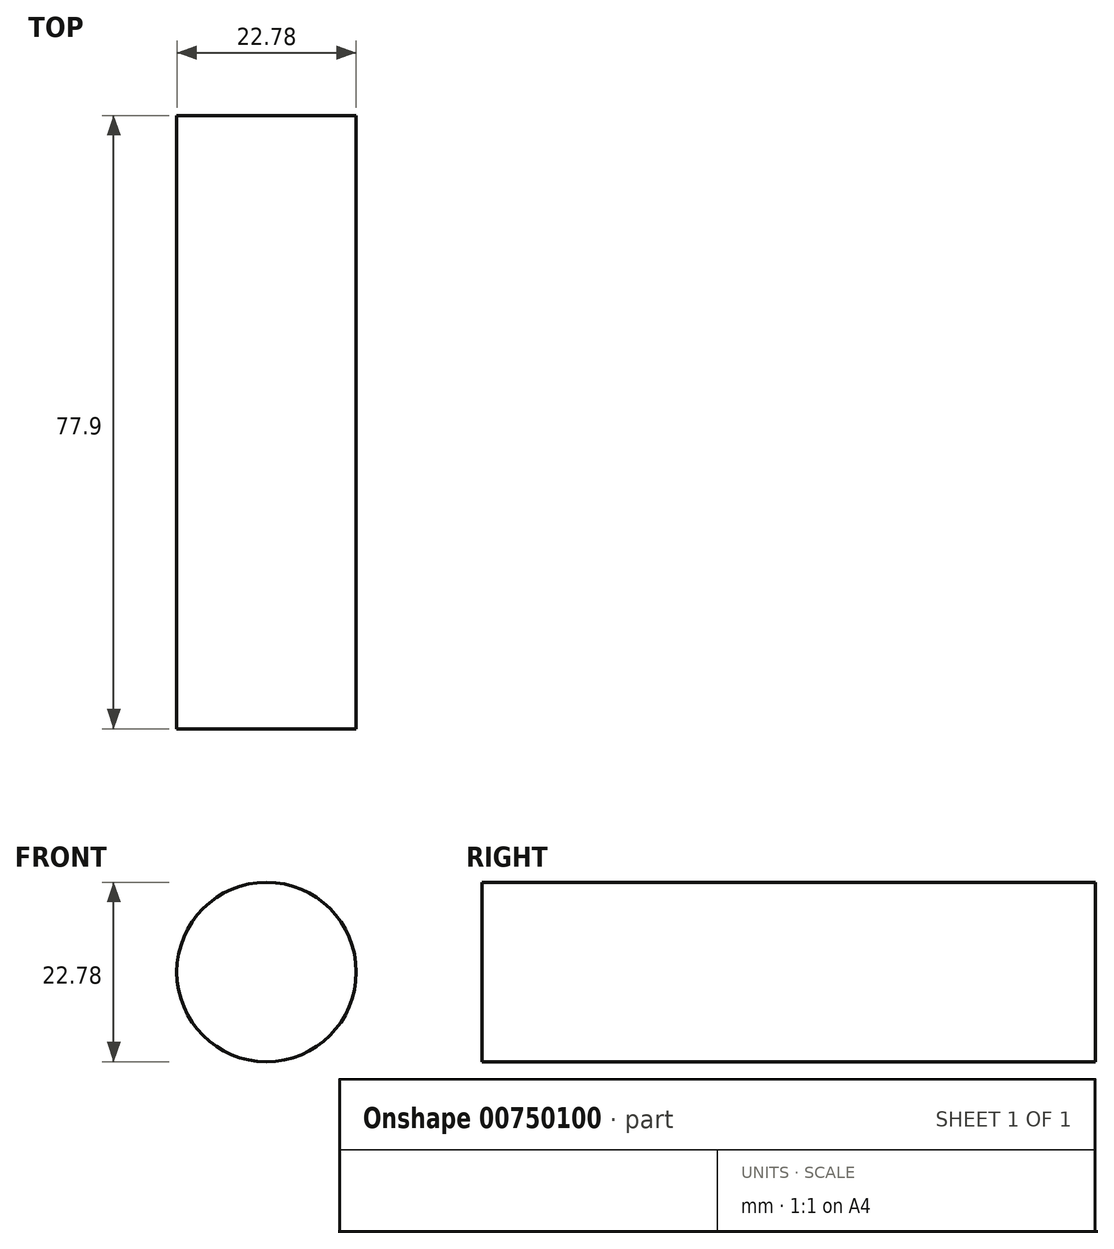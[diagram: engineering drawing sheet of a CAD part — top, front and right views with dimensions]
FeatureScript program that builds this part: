
annotation { "Feature Type Name" : "Feature", "Feature Type Description" : "" }
export const myFeature = defineFeature(function(context is Context, id is Id, definition is map)
    precondition{}
    {
        {
            var Q0;
            Q0=qCreatedBy(makeId("Front.planeOp"),FACE);
            var sketch = newSketch(context, id + "F0", { "sketchPlane" : qUnion([Q0])});
            skCircle(sketch, "E0", {"center": v(0, 0) * mm, "radius": 11.4 * mm});
            skSolve(sketch);
        }
        {
            var Q0;
            Q0=sQuery(id+"F0.wireOp",EDGE,"E0");
            extrude(context, id + "F1", {"bodyType" : ToolBodyType.SURFACE, "surfaceEntities" : qUnion([Q0]), "depth" : 77.9 * mm, "offsetDistance" : 25.4 * mm});
        }
    });
